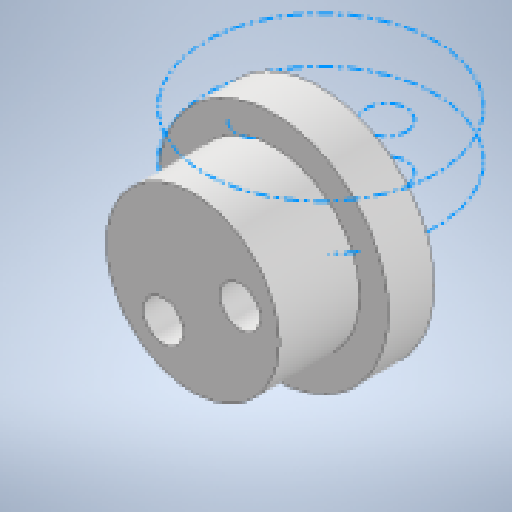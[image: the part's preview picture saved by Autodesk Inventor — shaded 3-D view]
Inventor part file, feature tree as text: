
AUTODESK INVENTOR PART (.ipt)
format: ipt  version: 2023 (Build 270158000, 158)  size: 157,184 bytes
history: native  units: in
note: dims shown in document units (in); Inventor stores cm internally (conversion verified against a paired STEP export)
features: reference x3, other x3, extrude x2, sketch x2, projected_geometry x1
ambient origin geometry x8: Origin, YZ Plane, XZ Plane, XY Plane, X Axis, Y Axis, Z Axis, Center Point
bodies: Solid1 (feature_tree)
feature tree (11):
  extrude  "Extrusion1"  Depth=0.0591in
  extrude  "Extrusion2"  Depth=0.2756in
  sketch  "Sketch3"  dims[d1=0.0591in d2=0.7874in]
  reference  "Reference1"
  reference  "Reference2"
  reference  "Reference3"
  sketch  "Sketch4"  dims[d4=0.1575in d5=0.0in d6=0.5906in d7=0.2756in d8=0.0in d9=0.315in]
  projected_geometry  "Projected Loop1"
  other  "<userpath>\OneDrive\Documents\Robotics Club\Cycloidal Drive\Drive.iam"
  other  "Drive.iam"
  other  "Shaft-1:1"
